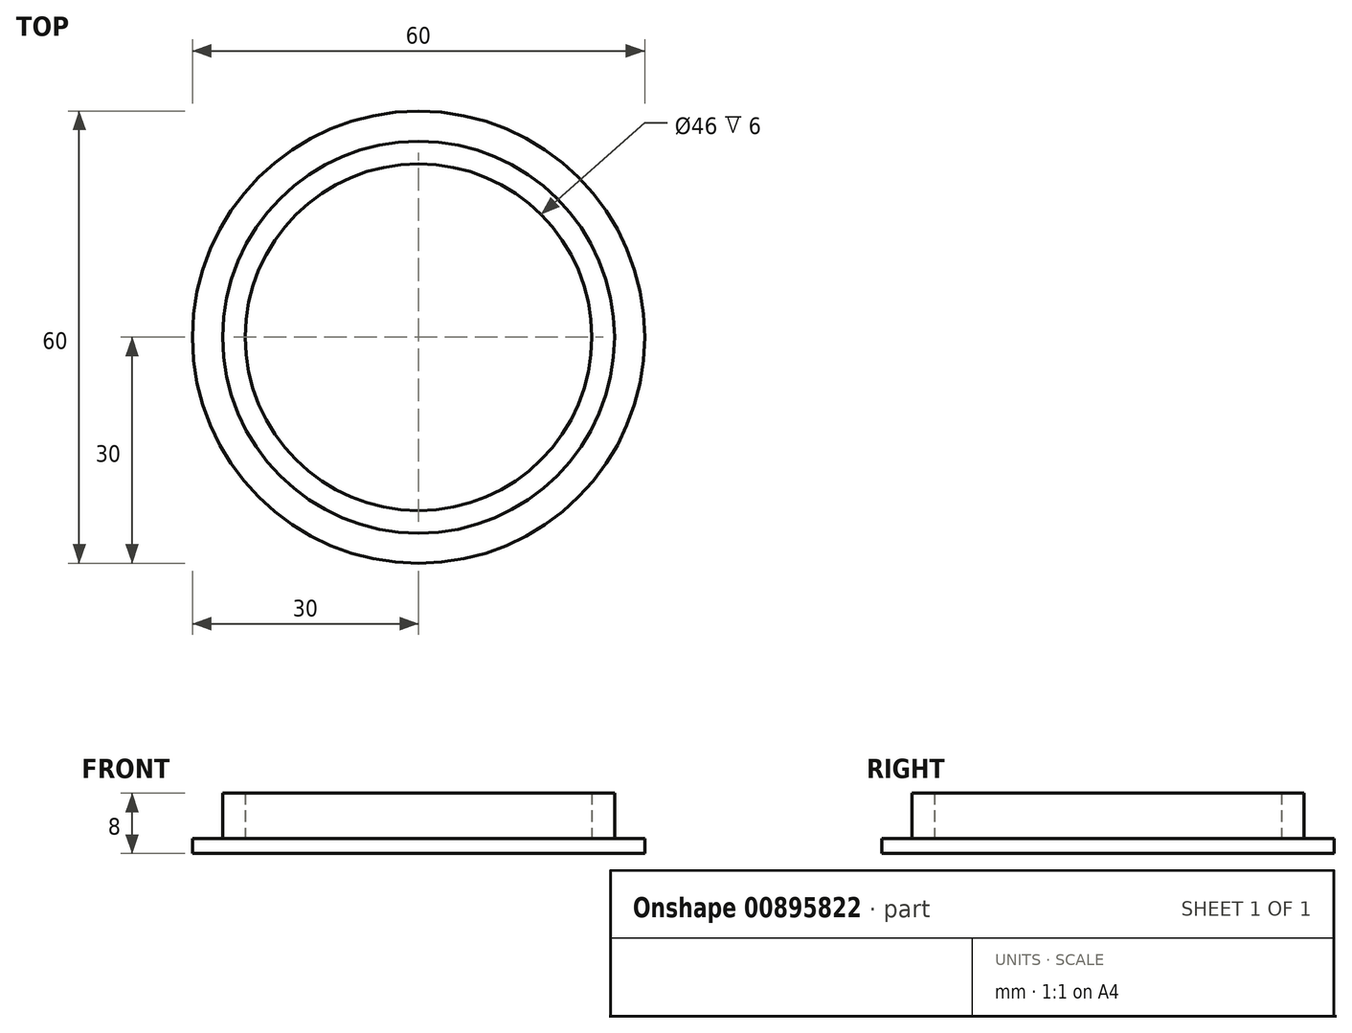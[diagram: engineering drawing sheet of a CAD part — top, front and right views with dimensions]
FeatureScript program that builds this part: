
annotation { "Feature Type Name" : "Feature", "Feature Type Description" : "" }
export const myFeature = defineFeature(function(context is Context, id is Id, definition is map)
    precondition{}
    {
        {
            var Q0;
            Q0=qCreatedBy(makeId("Top.planeOp"),FACE);
            var sketch = newSketch(context, id + "F0", { "sketchPlane" : qUnion([Q0])});
            skCircle(sketch, "E0", {"center": v(0, 0) * mm, "radius": 30 * mm});
            skSolve(sketch);
        }
        {
            var Q0;
            Q0=makeQuery(id+"F0.imprint","IMPRINT",FACE,{"disambiguationData":[TD([[makeQuery(id+"F0.imprint","IMPRINT",EDGE,{"derivedFrom":sQuery(id+"F0.wireOp",EDGE,"E0")}),1.0]])]});
            extrude(context, id + "F1", {"entities" : qUnion([Q0]), "depth" : 2 * mm, "offsetDistance" : 25 * mm});
        }
        {
            var Q0;
            Q0=qCreatedBy(makeId("Front.planeOp"),FACE);
            var sketch = newSketch(context, id + "F2", { "sketchPlane" : qUnion([Q0])});
            skLineSegment(sketch, "E1", {"start": v(23, 0) * mm, "end": v(23, 8) * mm});
            skLineSegment(sketch, "E2", {"start": v(23, 8) * mm, "end": v(26, 8) * mm});
            skLineSegment(sketch, "E3", {"start": v(26, 8) * mm, "end": v(26, 0) * mm});
            skLineSegment(sketch, "E4", {"start": v(26, 0) * mm, "end": v(23, 0) * mm});
            skLineSegment(sketch, "E5", {"start": v(0, 0) * mm, "end": v(0, 30.97) * mm, "construction": true});
            skSolve(sketch);
        }
        {
            var Q0;
            Q0 = qSketchRegion(id + "F2", true);
            var Q1;
            Q1=sQuery(id+"F2.wireOp",EDGE,"E5");
            revolve(context, id + "F3", {"operationType" : NewBodyOperationType.ADD, "surfaceOperationType" : NewSurfaceOperationType.NEW, "entities" : qUnion([Q0]), "axis" : qUnion([Q1]), "revolveType" : RevolveType.FULL});
        }
        {
            var Q0;
            Q0=qCreatedBy(makeId("Front.planeOp"),FACE);
            var sketch = newSketch(context, id + "F4", { "sketchPlane" : qUnion([Q0])});
            skCircle(sketch, "E6", {"center": v(27.95, 1.99) * mm, "radius": 1.35 * mm});
            skSolve(sketch);
        }
        {
            var Q0;
            Q0=sQuery(id+"F4.wireOp",EDGE,"E6");
            var Q1;
            Q1 = qConstructionFilter(qBodyType(qCreatedBy(id + "F2" ,EDGE), BodyType.WIRE), ConstructionObject.NO);
            var Q2;
            Q2=sQuery(id+"F2.wireOp",EDGE,"E5");
            revolve(context, id + "F5", {"bodyType" : ToolBodyType.SURFACE, "surfaceOperationType" : NewSurfaceOperationType.NEW, "surfaceEntities" : qUnion([Q0, Q1]), "axis" : qUnion([Q2]), "revolveType" : RevolveType.FULL});
        }
    });
